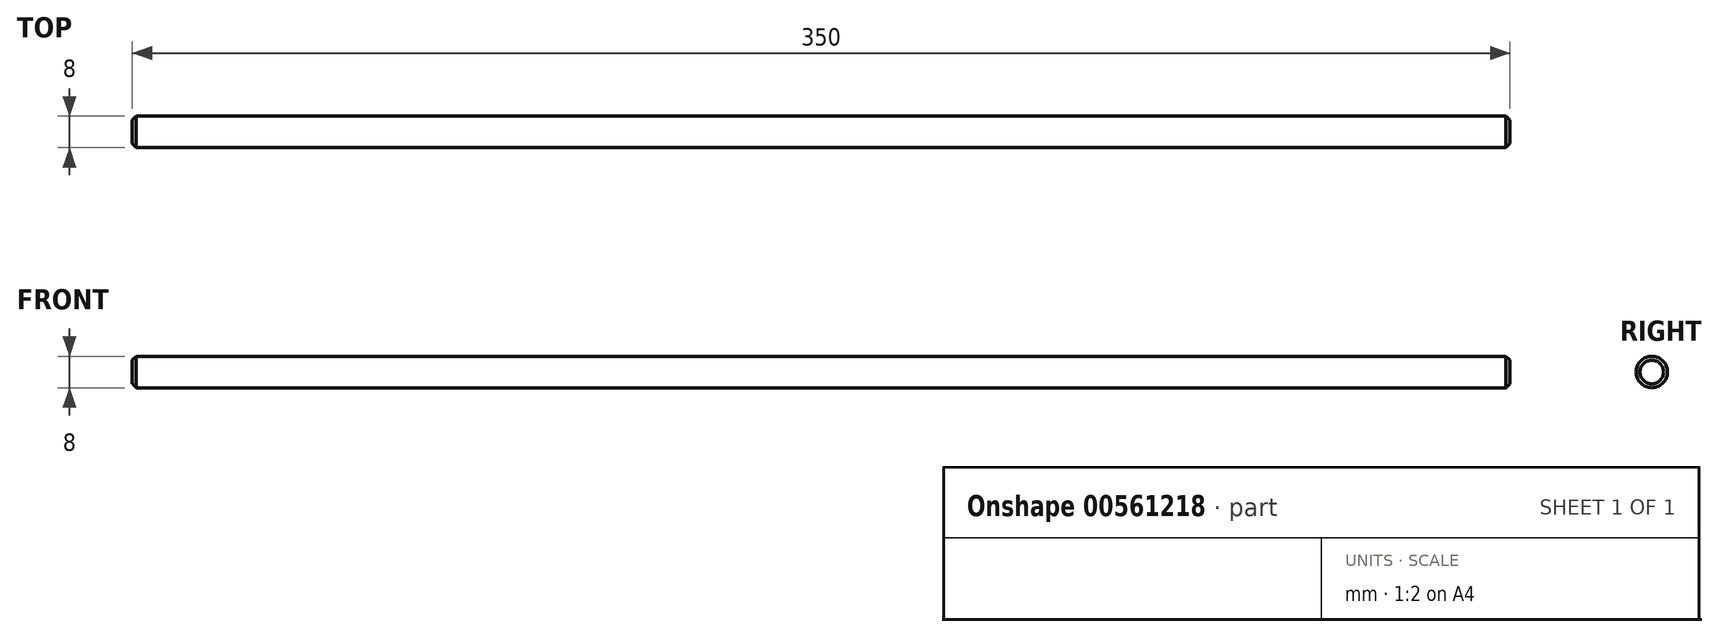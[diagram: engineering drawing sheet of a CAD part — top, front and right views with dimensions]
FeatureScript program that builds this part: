
annotation { "Feature Type Name" : "Feature", "Feature Type Description" : "" }
export const myFeature = defineFeature(function(context is Context, id is Id, definition is map)
    precondition{}
    {
        {
            var Q0;
            Q0=qCreatedBy(makeId("Right.planeOp"),FACE);
            var sketch = newSketch(context, id + "F0", { "sketchPlane" : qUnion([Q0])});
            skCircle(sketch, "E0", {"center": v(0, 0) * mm, "radius": 4 * mm});
            skSolve(sketch);
        }
        {
            var Q0;
            Q0 = qSketchRegion(id + "F0", true);
            extrude(context, id + "F1", {"entities" : qUnion([Q0]), "endBound" : BoundingType.SYMMETRIC, "depth" : 350 * mm, "offsetDistance" : 25 * mm});
        }
        {
            var Q0;
            Q0=makeQuery(id+"F1.opExtrude","CAP_EDGE",EDGE,{"disambiguationData":[OSD([sQuery(id+"F0.wireOp",EDGE,"E0")])],"isStart":false});
            var Q1;
            Q1=makeQuery(id+"F1.opExtrude","CAP_EDGE",EDGE,{"disambiguationData":[OSD([sQuery(id+"F0.wireOp",EDGE,"E0")])],"isStart":true});
            chamfer(context, id + "F2", {"entities" : qUnion([Q0, Q1]), "width" : 1 * mm, "tangentPropagation" : true});
        }
    });
